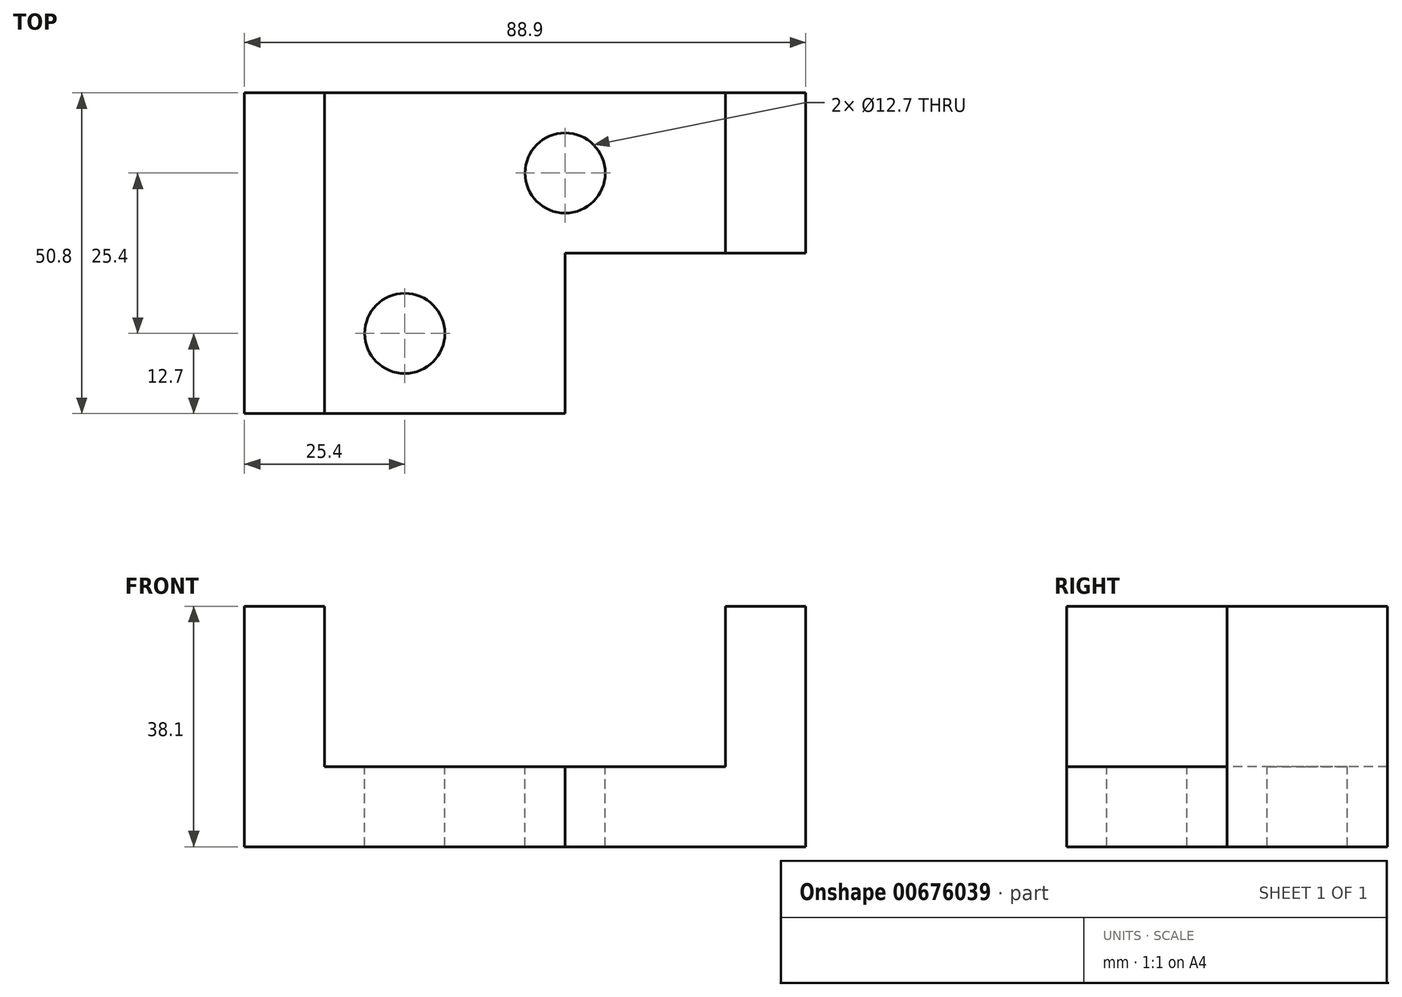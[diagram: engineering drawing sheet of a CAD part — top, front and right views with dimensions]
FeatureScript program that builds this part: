
annotation { "Feature Type Name" : "Feature", "Feature Type Description" : "" }
export const myFeature = defineFeature(function(context is Context, id is Id, definition is map)
    precondition{}
    {
        {
            var Q0;
            Q0=qCreatedBy(makeId("Front.planeOp"),FACE);
            var sketch = newSketch(context, id + "F0", { "sketchPlane" : qUnion([Q0])});
            skLineSegment(sketch, "E0.bottom", {"start": v(-44.45, 19.05) * mm, "end": v(44.45, 19.05) * mm});
            skLineSegment(sketch, "E0.top", {"start": v(-44.45, -19.05) * mm, "end": v(44.45, -19.05) * mm});
            skLineSegment(sketch, "E0.left", {"start": v(-44.45, 19.05) * mm, "end": v(-44.45, -19.05) * mm});
            skLineSegment(sketch, "E0.right", {"start": v(44.45, 19.05) * mm, "end": v(44.45, -19.05) * mm});
            skPoint(sketch, "E0.middle", {"position": v(0, 0) * mm});
            skSolve(sketch);
        }
        {
            var Q0;
            Q0=makeQuery(id+"F0.imprint","IMPRINT",FACE,{"disambiguationData":[TD([[makeQuery(id+"F0.imprint","IMPRINT",EDGE,{"derivedFrom":sQuery(id+"F0.wireOp",EDGE,"E0.bottom")}),-1.0]])]});
            extrude(context, id + "F1", {"entities" : qUnion([Q0]), "depth" : 50.8 * mm, "offsetDistance" : 25.4 * mm});
        }
        {
            var Q0;
            Q0=makeQuery(id+"F1.opExtrude","CAP_FACE",FACE,{"disambiguationData":[OSD([sQuery(id+"F0.wireOp",EDGE,"E0.bottom"),sQuery(id+"F0.wireOp",EDGE,"E0.top"),sQuery(id+"F0.wireOp",EDGE,"E0.left"),sQuery(id+"F0.wireOp",EDGE,"E0.right")])],"isStart":false});
            var sketch = newSketch(context, id + "F2", { "sketchPlane" : qUnion([Q0])});
            skLineSegment(sketch, "E1.bottom", {"start": v(-31.75, 19.05) * mm, "end": v(31.75, 19.05) * mm});
            skLineSegment(sketch, "E1.top", {"start": v(-31.75, -6.35) * mm, "end": v(31.75, -6.35) * mm});
            skLineSegment(sketch, "E1.left", {"start": v(-31.75, 19.05) * mm, "end": v(-31.75, -6.35) * mm});
            skLineSegment(sketch, "E1.right", {"start": v(31.75, 19.05) * mm, "end": v(31.75, -6.35) * mm});
            skSolve(sketch);
        }
        {
            var Q0;
            Q0=makeQuery(id+"F2.imprint","IMPRINT",FACE,{"disambiguationData":[TD([[makeQuery(id+"F2.imprint","IMPRINT",EDGE,{"derivedFrom":sQuery(id+"F2.wireOp",EDGE,"E1.bottom")}),-1.0]])]});
            extrude(context, id + "F3", {"entities" : qUnion([Q0]), "operationType" : NewBodyOperationType.REMOVE, "oppositeDirection" : true, "depth" : 50.8 * mm, "offsetDistance" : 25.4 * mm});
        }
        {
            var Q0;
            Q0=makeQuery(id+"F1.opExtrude","CAP_FACE",FACE,{"disambiguationData":[OSD([sQuery(id+"F0.wireOp",EDGE,"E0.bottom"),sQuery(id+"F0.wireOp",EDGE,"E0.top"),sQuery(id+"F0.wireOp",EDGE,"E0.left"),sQuery(id+"F0.wireOp",EDGE,"E0.right")])],"isStart":false});
            var sketch = newSketch(context, id + "F4", { "sketchPlane" : qUnion([Q0])});
            skLineSegment(sketch, "E2.bottom", {"start": v(6.35, -6.35) * mm, "end": v(44.45, -6.35) * mm});
            skLineSegment(sketch, "E2.top", {"start": v(6.35, -19.05) * mm, "end": v(44.45, -19.05) * mm});
            skLineSegment(sketch, "E2.left", {"start": v(6.35, -6.35) * mm, "end": v(6.35, -19.05) * mm});
            skLineSegment(sketch, "E2.right", {"start": v(44.45, -6.35) * mm, "end": v(44.45, -19.05) * mm});
            skLineSegment(sketch, "E3.bottom", {"start": v(31.75, 19.05) * mm, "end": v(44.45, 19.05) * mm});
            skLineSegment(sketch, "E3.top", {"start": v(31.75, -6.35) * mm, "end": v(44.45, -6.35) * mm});
            skLineSegment(sketch, "E3.left", {"start": v(31.75, 19.05) * mm, "end": v(31.75, -6.35) * mm});
            skLineSegment(sketch, "E3.right", {"start": v(44.45, 19.05) * mm, "end": v(44.45, -6.35) * mm});
            skSolve(sketch);
        }
        {
            var Q0;
            Q0=makeQuery(id+"F4.imprint","IMPRINT",FACE,{"disambiguationData":[TD([[makeQuery(id+"F4.imprint","IMPRINT",EDGE,{"derivedFrom":sQuery(id+"F4.wireOp",EDGE,"E2.bottom")}),-1.0]])]});
            extrude(context, id + "F5", {"entities" : qUnion([Q0]), "operationType" : NewBodyOperationType.REMOVE, "oppositeDirection" : true, "depth" : 25.4 * mm, "offsetDistance" : 25.4 * mm});
        }
        {
            var Q0;
            Q0=makeQuery(id+"F4.imprint","IMPRINT",FACE,{"disambiguationData":[TD([[makeQuery(id+"F4.imprint","IMPRINT",EDGE,{"derivedFrom":sQuery(id+"F4.wireOp",EDGE,"E3.bottom")}),-1.0]])]});
            extrude(context, id + "F6", {"entities" : qUnion([Q0]), "operationType" : NewBodyOperationType.REMOVE, "oppositeDirection" : true, "depth" : 25.4 * mm, "offsetDistance" : 25.4 * mm});
        }
        {
            var Q0;
            Q0=makeQuery(id+"F3.boolean.opBoolean","COPY",FACE,{"derivedFrom":makeQuery(id+"F3.opExtrude","SWEPT_FACE",FACE,{"disambiguationData":[OSD([sQuery(id+"F2.wireOp",EDGE,"E1.top")])]})});
            var sketch = newSketch(context, id + "F7", { "sketchPlane" : qUnion([Q0])});
            skCircle(sketch, "E4", {"center": v(-19.05, -38.1) * mm, "radius": 6.35 * mm});
            skSolve(sketch);
        }
        {
            var Q0;
            Q0=makeQuery(id+"F7.imprint","IMPRINT",FACE,{"disambiguationData":[TD([[makeQuery(id+"F7.imprint","IMPRINT",EDGE,{"derivedFrom":sQuery(id+"F7.wireOp",EDGE,"E4")}),1.0]])]});
            extrude(context, id + "F8", {"entities" : qUnion([Q0]), "operationType" : NewBodyOperationType.REMOVE, "oppositeDirection" : true, "depth" : 50.8 * mm, "offsetDistance" : 25.4 * mm});
        }
        {
            var Q0;
            Q0=makeQuery(id+"F3.boolean.opBoolean","COPY",FACE,{"derivedFrom":makeQuery(id+"F3.opExtrude","SWEPT_FACE",FACE,{"disambiguationData":[OSD([sQuery(id+"F2.wireOp",EDGE,"E1.top")])]})});
            var sketch = newSketch(context, id + "F9", { "sketchPlane" : qUnion([Q0])});
            skCircle(sketch, "E5", {"center": v(6.35, -12.7) * mm, "radius": 6.35 * mm});
            skSolve(sketch);
        }
        {
            var Q0;
            Q0=makeQuery(id+"F9.imprint","IMPRINT",FACE,{"disambiguationData":[TD([[makeQuery(id+"F9.imprint","IMPRINT",EDGE,{"derivedFrom":sQuery(id+"F9.wireOp",EDGE,"E5")}),1.0]])]});
            extrude(context, id + "F10", {"entities" : qUnion([Q0]), "operationType" : NewBodyOperationType.REMOVE, "oppositeDirection" : true, "depth" : 50.8 * mm, "offsetDistance" : 25.4 * mm});
        }
    });
